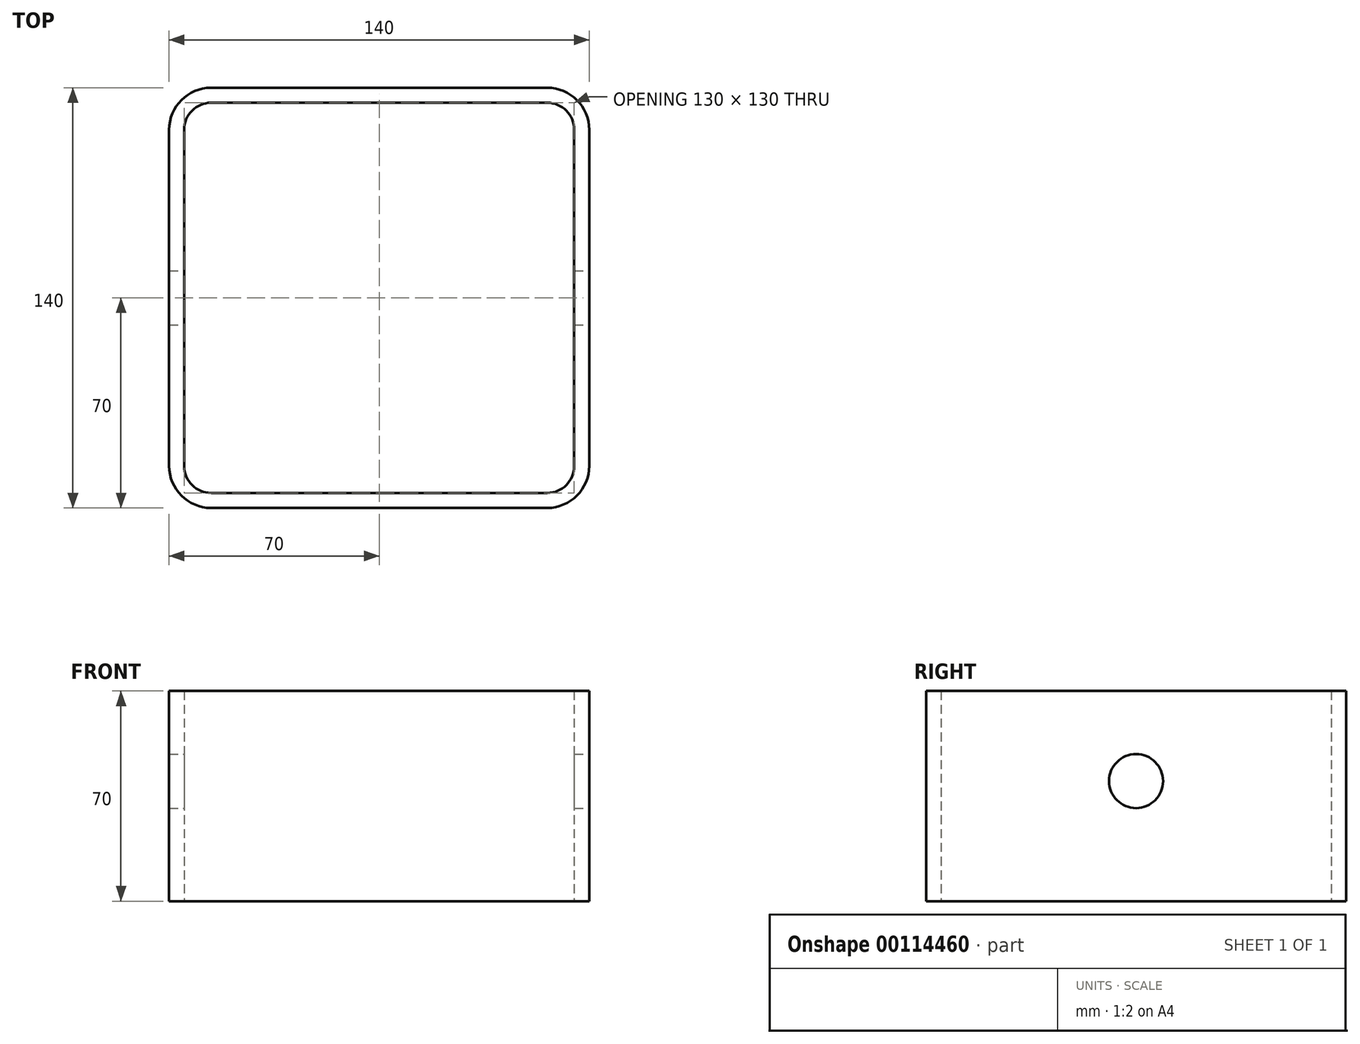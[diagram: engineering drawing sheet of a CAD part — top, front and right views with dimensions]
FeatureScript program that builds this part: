
annotation { "Feature Type Name" : "Feature", "Feature Type Description" : "" }
export const myFeature = defineFeature(function(context is Context, id is Id, definition is map)
    precondition{}
    {
        {
            var Q0;
            Q0=qCreatedBy(makeId("Top.planeOp"),FACE);
            var sketch = newSketch(context, id + "F0", { "sketchPlane" : qUnion([Q0])});
            skLineSegment(sketch, "E0.bottom", {"start": v(56, -70) * mm, "end": v(-56, -70) * mm});
            skLineSegment(sketch, "E0.top", {"start": v(56, 70) * mm, "end": v(-56, 70) * mm});
            skLineSegment(sketch, "E0.left", {"start": v(70, -56) * mm, "end": v(70, 56) * mm});
            skLineSegment(sketch, "E0.right", {"start": v(-70, -56) * mm, "end": v(-70, 56) * mm});
            skPoint(sketch, "E0.middle", {"position": v(0, 0) * mm});
            skPoint(sketch, "E1.visualSharp", {"position": v(-70, 70) * mm});
            skArc(sketch, "E1.filletArc", {"start": v(-56, 70) * mm, "mid": v(-65.9, 65.9) * mm, "end": v(-70, 56) * mm});
            skPoint(sketch, "E2.visualSharp", {"position": v(70, 70) * mm});
            skArc(sketch, "E2.filletArc", {"start": v(70, 56) * mm, "mid": v(65.9, 65.9) * mm, "end": v(56, 70) * mm});
            skPoint(sketch, "E3.visualSharp", {"position": v(70, -70) * mm});
            skArc(sketch, "E3.filletArc", {"start": v(56, -70) * mm, "mid": v(65.9, -65.9) * mm, "end": v(70, -56) * mm});
            skPoint(sketch, "E4.visualSharp", {"position": v(-70, -70) * mm});
            skArc(sketch, "E4.filletArc", {"start": v(-70, -56) * mm, "mid": v(-65.9, -65.9) * mm, "end": v(-56, -70) * mm});
            skArc(sketch, "E5.0", {"start": v(-65, -56) * mm, "mid": v(-62.36, -62.36) * mm, "end": v(-56, -65) * mm});
            skLineSegment(sketch, "E5.1", {"start": v(56, -65) * mm, "end": v(-56, -65) * mm});
            skLineSegment(sketch, "E5.2", {"start": v(-65, -56) * mm, "end": v(-65, 56) * mm});
            skArc(sketch, "E5.3", {"start": v(56, -65) * mm, "mid": v(62.36, -62.36) * mm, "end": v(65, -56) * mm});
            skArc(sketch, "E5.4", {"start": v(-56, 65) * mm, "mid": v(-62.36, 62.36) * mm, "end": v(-65, 56) * mm});
            skLineSegment(sketch, "E5.5", {"start": v(56, 65) * mm, "end": v(-56, 65) * mm});
            skArc(sketch, "E5.6", {"start": v(65, 56) * mm, "mid": v(62.36, 62.36) * mm, "end": v(56, 65) * mm});
            skLineSegment(sketch, "E5.7", {"start": v(65, -56) * mm, "end": v(65, 56) * mm});
            skSolve(sketch);
        }
        {
            var Q0;
            Q0=makeQuery(id+"F0.imprint","IMPRINT",FACE,{"disambiguationData":[TD([[makeQuery(id+"F0.imprint","IMPRINT",EDGE,{"derivedFrom":sQuery(id+"F0.wireOp",EDGE,"E0.bottom")}),-1.0]])]});
            extrude(context, id + "F1", {"entities" : qUnion([Q0]), "depth" : 70 * mm});
        }
        {
            var Q0;
            Q0=makeQuery(id+"F1.opExtrude","SWEPT_FACE",FACE,{"disambiguationData":[OSD([sQuery(id+"F0.wireOp",EDGE,"E0.left")])]});
            var sketch = newSketch(context, id + "F2", { "sketchPlane" : qUnion([Q0])});
            skCircle(sketch, "E6", {"center": v(0, 40) * mm, "radius": 9 * mm});
            skSolve(sketch);
        }
        {
            var Q0;
            Q0=makeQuery(id+"F2.imprint","IMPRINT",FACE,{"disambiguationData":[TD([[makeQuery(id+"F2.imprint","IMPRINT",EDGE,{"derivedFrom":sQuery(id+"F2.wireOp",EDGE,"E6")}),1.0]])]});
            extrude(context, id + "F3", {"entities" : qUnion([Q0]), "operationType" : NewBodyOperationType.REMOVE, "endBound" : BoundingType.THROUGH_ALL, "oppositeDirection" : true, "depth" : 25 * mm});
        }
    });
